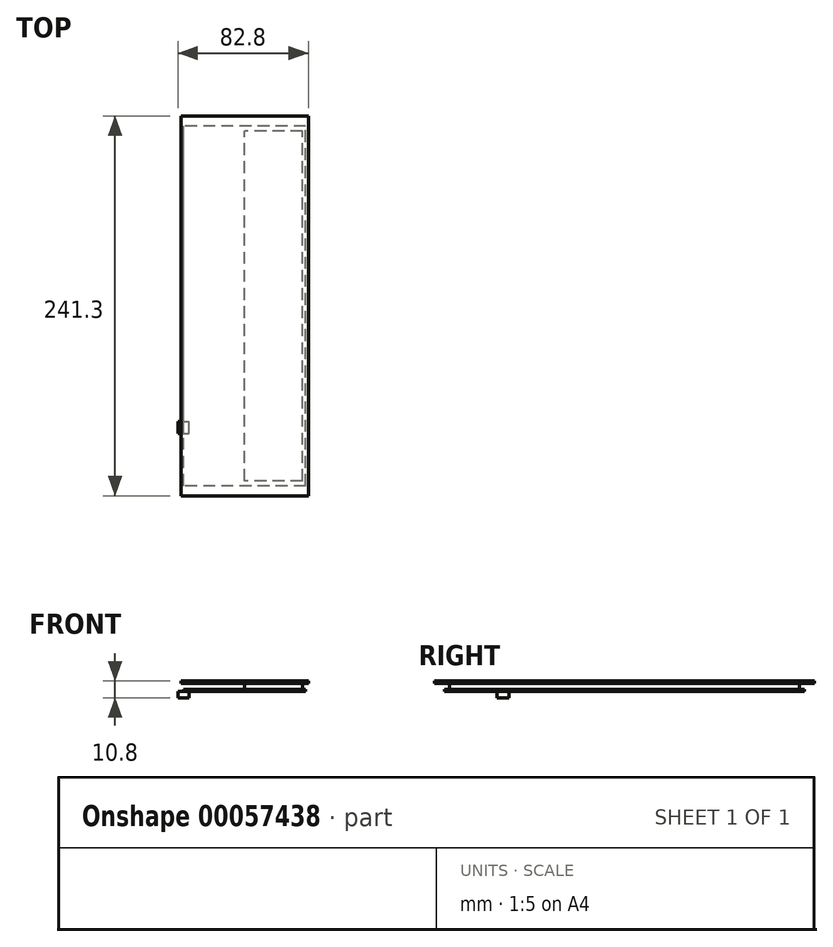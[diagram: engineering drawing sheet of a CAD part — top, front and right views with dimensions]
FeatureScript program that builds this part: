
annotation { "Feature Type Name" : "Feature", "Feature Type Description" : "" }
export const myFeature = defineFeature(function(context is Context, id is Id, definition is map)
    precondition{}
    {
        {
            var Q0;
            Q0=qCreatedBy(makeId("Front.planeOp"),FACE);
            var sketch = newSketch(context, id + "F0", { "sketchPlane" : qUnion([Q0])});
            skLineSegment(sketch, "E0.bottom", {"start": v(-27.1, 15.54) * mm, "end": v(13.4, 15.54) * mm});
            skLineSegment(sketch, "E0.top", {"start": v(-27.1, 14.04) * mm, "end": v(13.4, 14.04) * mm});
            skLineSegment(sketch, "E0.left", {"start": v(-27.1, 15.54) * mm, "end": v(-27.1, 14.04) * mm});
            skLineSegment(sketch, "E0.right", {"start": v(13.4, 15.54) * mm, "end": v(13.4, 14.04) * mm});
            skLineSegment(sketch, "E1.bottom", {"start": v(-23.4, 14.04) * mm, "end": v(13.4, 14.04) * mm});
            skLineSegment(sketch, "E1.top", {"start": v(-23.4, 10.24) * mm, "end": v(13.4, 10.24) * mm});
            skLineSegment(sketch, "E1.left", {"start": v(-23.4, 14.04) * mm, "end": v(-23.4, 10.24) * mm});
            skLineSegment(sketch, "E1.right", {"start": v(13.4, 14.04) * mm, "end": v(13.4, 10.24) * mm});
            skLineSegment(sketch, "E2.bottom", {"start": v(-25.4, 10.24) * mm, "end": v(13.4, 10.24) * mm});
            skLineSegment(sketch, "E2.top", {"start": v(-25.4, 8.74) * mm, "end": v(13.4, 8.74) * mm});
            skLineSegment(sketch, "E2.left", {"start": v(-25.4, 10.24) * mm, "end": v(-25.4, 8.74) * mm});
            skLineSegment(sketch, "E2.right", {"start": v(13.4, 10.24) * mm, "end": v(13.4, 8.74) * mm});
            skLineSegment(sketch, "E3", {"start": v(-23.4, 14.04) * mm, "end": v(-27.1, 14.04) * mm});
            skLineSegment(sketch, "E4", {"start": v(13.4, 8.74) * mm, "end": v(13.4, 28.68) * mm});
            skLineSegment(sketch, "E5.MirrorCS", {"start": v(52.2, 10.24) * mm, "end": v(52.2, 8.74) * mm});
            skLineSegment(sketch, "E6.MirrorCS", {"start": v(50.2, 14.04) * mm, "end": v(53.9, 14.04) * mm});
            skLineSegment(sketch, "E7.MirrorCS", {"start": v(50.2, 14.04) * mm, "end": v(50.2, 10.24) * mm});
            skLineSegment(sketch, "E8.MirrorCS", {"start": v(53.9, 15.54) * mm, "end": v(53.9, 14.04) * mm});
            skLineSegment(sketch, "E9.MirrorCS", {"start": v(53.9, 15.54) * mm, "end": v(13.4, 15.54) * mm});
            skLineSegment(sketch, "E10.MirrorCS", {"start": v(50.2, 14.04) * mm, "end": v(13.4, 14.04) * mm});
            skLineSegment(sketch, "E11.MirrorCS", {"start": v(52.2, 10.24) * mm, "end": v(13.4, 10.24) * mm});
            skLineSegment(sketch, "E12.MirrorCS", {"start": v(52.2, 8.74) * mm, "end": v(13.4, 8.74) * mm});
            skLineSegment(sketch, "E13", {"start": v(13.4, 8.74) * mm, "end": v(13.4, 3.2) * mm});
            skSolve(sketch);
        }
        {
            var Q0;
            {var subQ0=sQuery(id+"F0.wireOp",EDGE,"E5.MirrorCS");Q0=makeQuery(id+"F0.imprint","IMPRINT",FACE,{"disambiguationData":[TD([[makeQuery(id+"F0.imprint","IMPRINT",EDGE,{"derivedFrom":subQ0}),-1.0]])]});}
            var Q1;
            {var subQ1=sQuery(id+"F0.wireOp",EDGE,"E2.top");Q1=makeQuery(id+"F0.imprint","IMPRINT",FACE,{"disambiguationData":[TD([[makeQuery(id+"F0.imprint","IMPRINT",EDGE,{"derivedFrom":subQ1}),1.0]])]});}
            extrude(context, id + "F1", {"entities" : qUnion([Q0, Q1]), "endBound" : BoundingType.SYMMETRIC, "depth" : 228.6 * mm});
        }
        {
            var Q0;
            {var subQ1=sQuery(id+"F0.wireOp",EDGE,"E0.bottom");Q0=makeQuery(id+"F0.imprint","IMPRINT",FACE,{"disambiguationData":[TD([[makeQuery(id+"F0.imprint","IMPRINT",EDGE,{"derivedFrom":subQ1}),-1.0]])]});}
            var Q1;
            {var subQ1=sQuery(id+"F0.wireOp",EDGE,"E9.MirrorCS");Q1=makeQuery(id+"F0.imprint","IMPRINT",FACE,{"disambiguationData":[TD([[makeQuery(id+"F0.imprint","IMPRINT",EDGE,{"derivedFrom":subQ1}),1.0]])]});}
            extrude(context, id + "F2", {"entities" : qUnion([Q0, Q1]), "endBound" : BoundingType.SYMMETRIC, "depth" : 241.3 * mm});
        }
        {
            var Q0;
            {var subQ0=sQuery(id+"F0.wireOp",EDGE,"E1.bottom");Q0=makeQuery(id+"F0.imprint","IMPRINT",FACE,{"disambiguationData":[TD([[makeQuery(id+"F0.imprint","IMPRINT",EDGE,{"derivedFrom":subQ0}),-1.0]])]});}
            var Q1;
            {var subQ0=sQuery(id+"F0.wireOp",EDGE,"E10.MirrorCS");Q1=makeQuery(id+"F0.imprint","IMPRINT",FACE,{"disambiguationData":[TD([[makeQuery(id+"F0.imprint","IMPRINT",EDGE,{"derivedFrom":subQ0}),1.0]])]});}
            extrude(context, id + "F3", {"entities" : qUnion([Q0, Q1]), "endBound" : BoundingType.SYMMETRIC, "depth" : 222.25 * mm});
        }
        {
            var Q0;
            Q0=makeQuery(id+"F1.opExtrude","SWEPT_FACE",FACE,{"disambiguationData":[OSD([sQuery(id+"F0.wireOp",EDGE,"E2.top"),sQuery(id+"F0.wireOp",EDGE,"E12.MirrorCS")])]});
            var sketch = newSketch(context, id + "F4", { "sketchPlane" : qUnion([Q0])});
            skLineSegment(sketch, "E14.bottom", {"start": v(-28.9, 81) * mm, "end": v(-21.9, 81) * mm});
            skLineSegment(sketch, "E14.top", {"start": v(-28.9, 73.3) * mm, "end": v(-21.9, 73.3) * mm});
            skLineSegment(sketch, "E14.left", {"start": v(-28.9, 81) * mm, "end": v(-28.9, 73.3) * mm});
            skLineSegment(sketch, "E14.right", {"start": v(-21.9, 81) * mm, "end": v(-21.9, 73.3) * mm});
            skSolve(sketch);
        }
        {
            var Q0;
            {var subQ0=sQuery(id+"F4.wireOp",EDGE,"E14.right");Q0=makeQuery(id+"F4.imprint","IMPRINT",FACE,{"disambiguationData":[TD([[makeQuery(id+"F4.imprint","IMPRINT",EDGE,{"derivedFrom":subQ0}),-1.0]])]});}
            var Q1;
            {var subQ0=sQuery(id+"F4.wireOp",EDGE,"E14.left");Q1=makeQuery(id+"F4.imprint","IMPRINT",FACE,{"disambiguationData":[TD([[makeQuery(id+"F4.imprint","IMPRINT",EDGE,{"derivedFrom":subQ0}),1.0]])]});}
            extrude(context, id + "F5", {"entities" : qUnion([Q0, Q1]), "operationType" : NewBodyOperationType.ADD, "depth" : 4 * mm});
        }
    });
